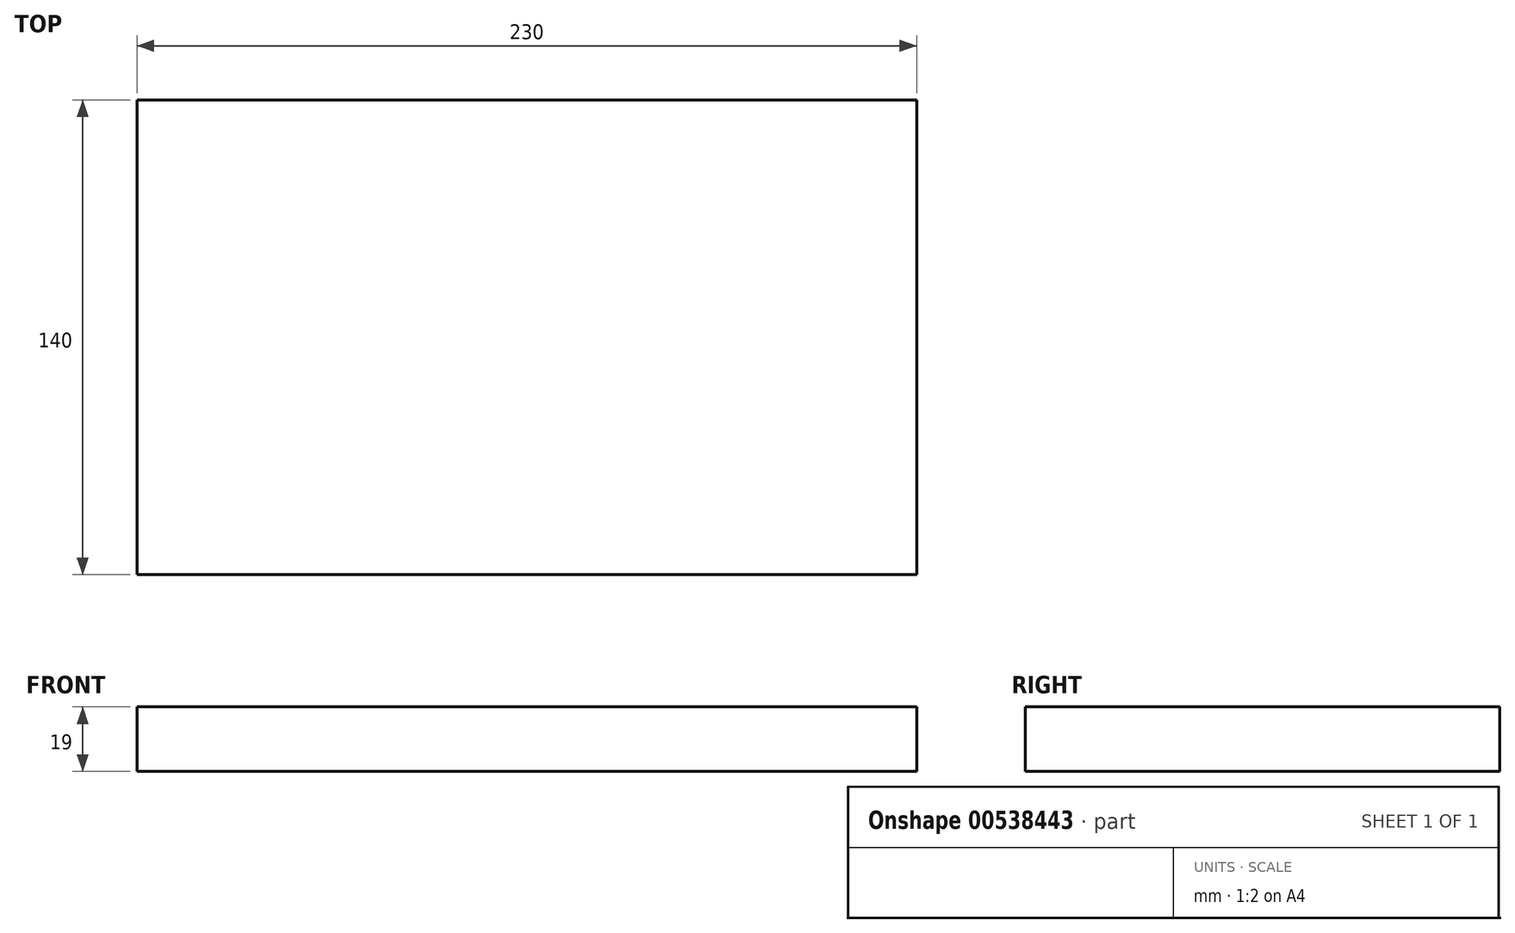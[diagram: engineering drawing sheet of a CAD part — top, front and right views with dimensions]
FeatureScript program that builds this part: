
annotation { "Feature Type Name" : "Feature", "Feature Type Description" : "" }
export const myFeature = defineFeature(function(context is Context, id is Id, definition is map)
    precondition{}
    {
        {
            var Q0;
            Q0=qCreatedBy(makeId("Top.planeOp"),FACE);
            var sketch = newSketch(context, id + "F0", { "sketchPlane" : qUnion([Q0])});
            skLineSegment(sketch, "E0.bottom", {"start": v(115, 70) * mm, "end": v(-115, 70) * mm});
            skLineSegment(sketch, "E0.top", {"start": v(115, -70) * mm, "end": v(-115, -70) * mm});
            skLineSegment(sketch, "E0.left", {"start": v(115, 70) * mm, "end": v(115, -70) * mm});
            skLineSegment(sketch, "E0.right", {"start": v(-115, 70) * mm, "end": v(-115, -70) * mm});
            skPoint(sketch, "E0.middle", {"position": v(0, 0) * mm});
            skSolve(sketch);
        }
        {
            var Q0;
            Q0=makeQuery(id+"F0.imprint","IMPRINT",FACE,{"disambiguationData":[TD([[makeQuery(id+"F0.imprint","IMPRINT",EDGE,{"derivedFrom":sQuery(id+"F0.wireOp",EDGE,"E0.bottom")}),1.0]])]});
            extrude(context, id + "F1", {"entities" : qUnion([Q0]), "depth" : 19 * mm, "offsetDistance" : 25 * mm});
        }
    });
